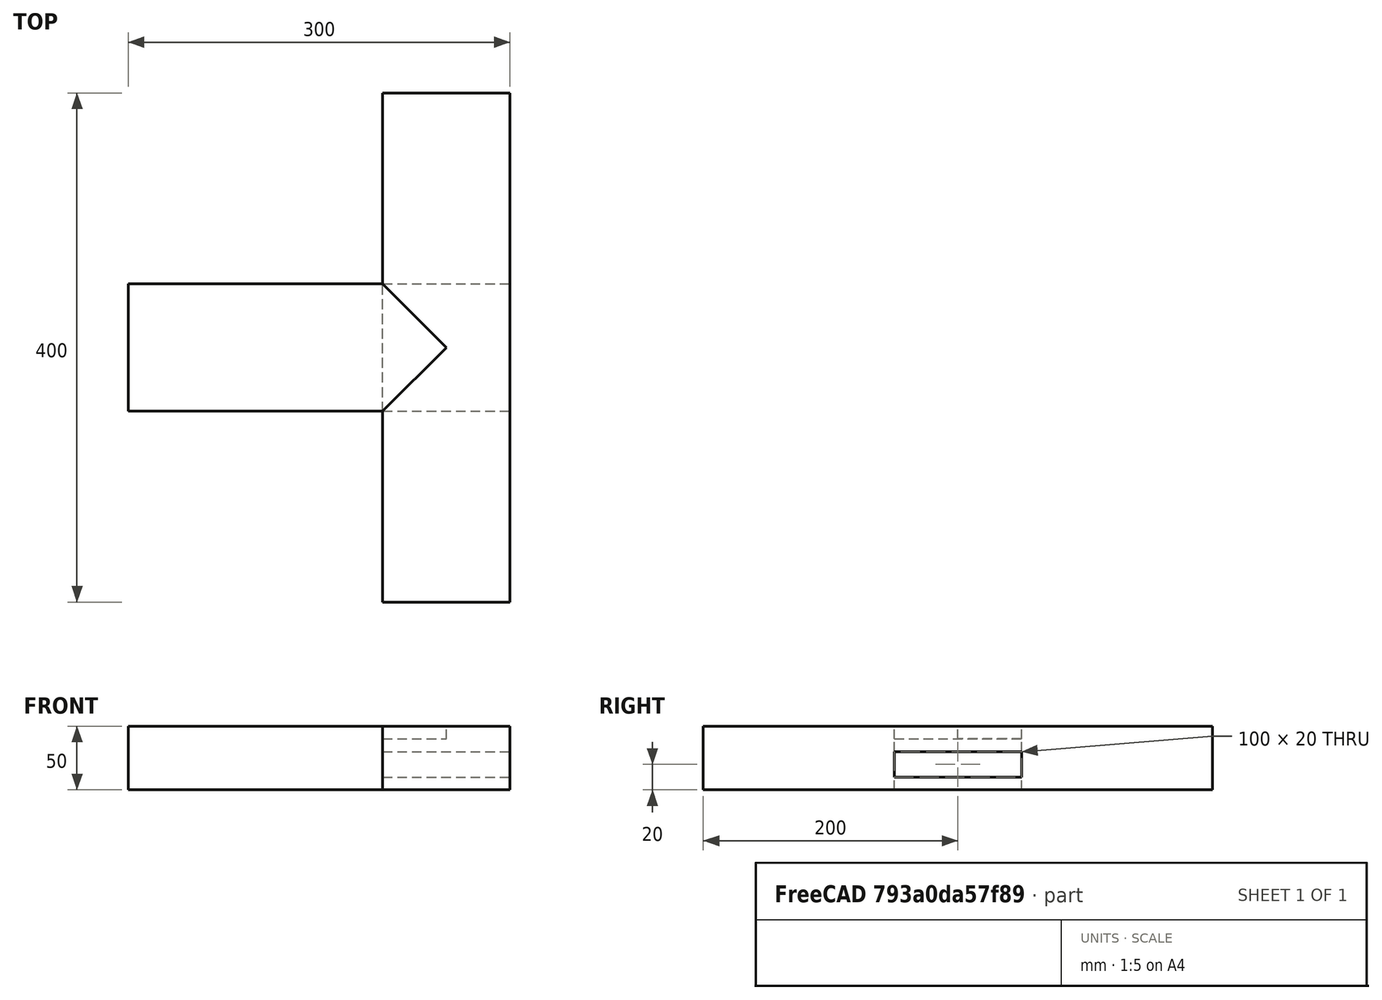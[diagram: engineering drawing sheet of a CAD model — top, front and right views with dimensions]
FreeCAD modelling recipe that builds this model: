
FCSTD DOCUMENT  (FreeCAD 0.19R16207 (Git))
Label: EMENDA T
License: All rights reserved
LicenseURL: http://en.wikipedia.org/wiki/All_rights_reserved
objects: Part::Box×4, Part::Feature×3, Part::MultiFuse×1, Part::Cut×1
note: 9 computed .brp shape members not serialized (recipe doc carries the construction recipe); baked Part::Feature solids carry a one-line shape summary decoded from their .brp

FEATURE [Part::Box] Box  label="Cube"
  AttacherType = Attacher::AttachEngine3D
  Height = 50
  Length = 200
  Placement = pos=(6.1e-15,50,0) rot=(0,0,1;3.14159rad)
  Width = 100
FEATURE [Part::Box] Box001  label="Cube001"
  AttacherType = Attacher::AttachEngine3D
  Height = 10
  Length = 70.7107
  Placement = pos=(-50,0,40) rot=(0,0,1;5.49779rad)
  Width = 70.7107
FEATURE [Part::Box] Box002  label="Cube002"
  AttacherType = Attacher::AttachEngine3D
  Height = 20
  Length = 100
  Placement = pos=(0,-50,10) rot=(0,0,1;0rad)
  Width = 100
FEATURE [Part::MultiFuse] Fusion
  Shapes = -> [Box,Box001,Box002]
FEATURE [Part::Feature] Fusion001
  shape: bbox 300 x 100 x 50 mm, 15 faces (baked)
FEATURE [Part::Box] Box003  label="Cube003"
  AttacherType = Attacher::AttachEngine3D
  Height = 50
  Length = 100
  Placement = pos=(0,-200,0) rot=(0,0,1;0rad)
  Width = 400
FEATURE [Part::Cut] Cut
  Base = -> Box003
  Tool = -> Fusion001
FEATURE [Part::Feature] Cut001
  shape: bbox 100 x 400 x 50 mm, 15 faces (baked)
FEATURE [Part::Feature] Fusion001001  label="Fusion002"
  shape: bbox 300 x 100 x 50 mm, 15 faces (baked)
